# Revit family: 201_MAK+KL-_
name_source: partatom
category: Air Terminals
units: mm (PartAtom-declared; Revit-internal decimal feet)

## family parameters
Always vertical = Yes
Cut with Voids When Loaded = No
Part Type = Normal
Room Calculation Point = Yes
Round Connector Dimension = Use Diameter
Shared = No
Work Plane-Based = No

## types (4) — shared parameters
AA1 = 298 mm
AA2 = 298 mm
B = 450 mm  [stored 1.47638 ft]
B1 = 358 mm  [stored 1.17454 ft]
BOX0 = Yes
BOX1 = No
B__ve = -450 mm  [stored -1.47638 ft]
C = 92 mm  [stored 0.301837 ft]
CAT0 = Yes
CAT1 = No
CAT2 = Yes
Description = Round nozzle diffuser
H = 140 mm  [stored 0.459318 ft]
H2 = 33 mm
H3 = 107 mm
H4 = 8 mm  [stored 0.0262467 ft]
H4__ve = -8 mm  [stored -0.0262467 ft]
H5 = 10 mm  [stored 0.0328084 ft]
H6 = 70 mm  [stored 0.229659 ft]
L_ARR = 400 mm  [stored 1.31234 ft]
Manufacturer = Climecon
QmdConnectorList = 201;D
URL = www.climecon.fi
W1 = 135 mm  [stored 0.442913 ft]
WW1 = 103 mm
W_ARR = 400 mm  [stored 1.31234 ft]
XRefLineVPlnId = 7453
YRefLineVPlnId = 7456
magiPartTypeId = 201
magiProductFamilyId = MAK+KL-*
zero-valued in all types: H_ARR, MC_Default_elevation

## per-type parameters (varying)
| type | CLBTZ | CLBTZ_End__ve | CLBTZ__ve | CLD | CL_Location_5000 | D | D1 | H1 | R | R1 | R2 |
| MAK+KL-125 | 30 mm  [stored 0.0984252 ft] | -40 mm  [stored -0.131234 ft] | -30 mm  [stored -0.0984252 ft] | 160 mm  [stored 0.524934 ft] | 5030 mm  [stored 16.5026 ft] | 125 mm | 340 mm  [stored 1.11549 ft] | 40 mm  [stored 0.131234 ft] | 63 mm | 132 mm | 170 mm  [stored 0.557743 ft] |
| MAK+KL-250 | 50 mm  [stored 0.164042 ft] | -60 mm | -50 mm  [stored -0.164042 ft] | 250 mm  [stored 0.82021 ft] | 5050 mm | 250 mm | 520 mm  [stored 1.70604 ft] | 60 mm  [stored 0.19685 ft] | 125 mm  [stored 0.410105 ft] | 208 mm | 260 mm  [stored 0.853018 ft] |
| MAK+KL-200 | 40 mm  [stored 0.131234 ft] | -50 mm  [stored -0.164042 ft] | -40 mm  [stored -0.131234 ft] | 250 mm  [stored 0.82021 ft] | 5040 mm | 200 mm | 430 mm  [stored 1.41076 ft] | 50 mm  [stored 0.164042 ft] | 100 mm  [stored 0.328084 ft] | 170 mm  [stored 0.557743 ft] | 215 mm  [stored 0.705381 ft] |
| MAK+KL-160 | 30 mm  [stored 0.0984252 ft] | -40 mm  [stored -0.131234 ft] | -30 mm  [stored -0.0984252 ft] | 200 mm  [stored 0.656168 ft] | 5030 mm  [stored 16.5026 ft] | 160 mm | 340 mm  [stored 1.11549 ft] | 40 mm  [stored 0.131234 ft] | 80 mm  [stored 0.262467 ft] | 132 mm | 170 mm  [stored 0.557743 ft] |

note: column(s) folded — value = type name in every type: magiProductCode, magiProductId

note: [stored X ft] marks values corroborated as IEEE doubles in the binary element streams (Revit-internal decimal feet)
